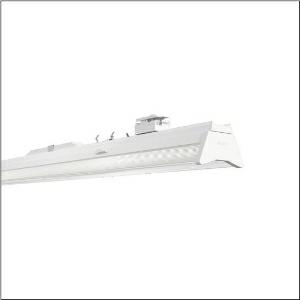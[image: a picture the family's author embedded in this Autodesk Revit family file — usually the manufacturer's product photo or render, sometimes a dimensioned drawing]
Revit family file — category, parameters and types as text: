
# Revit family: licross_21_performance_mo_52tm16dn445g
name_source: partatom
category: Lighting Fixtures
units: mm (PartAtom-declared; Revit-internal decimal feet)

## family parameters
Cut with Voids When Loaded = No
Host = Face
Light Source = No
Part Type = Normal
Room Calculation Point = No
Round Connector Dimension = Use Diameter
Shared = No

## types (1)
- --- (1 x LED, 4500 lm, 24.9 W, 4000K)
    Apparent Load = 25 VA
    CIE Flux Codes = 66 88 96 79 100
    Color Rendering = 80
    Color Temperature = 4000K
    Default Elevation = 1800 mm
    Description = Licross 21 Performance MO, luminaire insert, of sheet steel, galvanised, coil coated, white, length: 1.500mm, width: 120mm, height: 123mm, LED rated luminous flux: 4.500lm, light colour: 840, SDCM (Standard Deviation of Colour Matching)MacAdam ≤ 3 SDCM (initial), control gear: DALI 2, with plug, 5-pole, with phase selection, mains connection: 220..240V, AC, 50/60Hz, rated input power: 25W, internal wiring halogen-free, primary light control with lens, of plastic, primary optical cover: cover, of PMMA, CAT 2 (L<= 3000cd/m²), light emission: direct/indirect distribution, primary light characteristic: symmetric, protection rating (complete): IP40, insulation class (complete): insulation class I (protective earthing), certification: CE, ENEC, UKCA, protection symbol: D if used in an environment without relevant dust loads with corresponding accessories, impact resistance: IK06, permissible ambient temperature for indoor applications: -25..+50°C, corresponds to IFS (International Featured Standards) requirements for safety and quality in the food industry, reducing of maximum allowable ambient temperature of 5°C with ceiling mounting, LABS conformity tested according to VDMA 24364:2018-05, The light source and the operating device comply with the requirements of the Ecodesign Regulation (EU) 2019/2020 and are replaceable in accordance with this regulation, packaging unit: 1 piece
    Height = 114 mm
    Lamp = 1 x LED
    Lamp Light Flux = 4500 lm
    Lamp Power = 24.9 W
    Lamp count = 1
    Length = 1500 mm
    Luminous efficacy = 181 lm/W
    Manufacturer = Siteco
    ModVariant = No
    Model = 52TM16DN445G
    Mounting Place = Ceiling
    Mounting Type = Pendant
    Number of Poles = 1
    OnlyDefault = Yes
    Power Factor = 1
    Product Name = Licross 21 Performance MO
    Product group = luminaire insert | ceiling pendant
    ProductGroupID = 901
    Protection Class = Protection class I
    Protection Degree = IP 40
    RLX_Detail_Level = 1
    RLX_Emergency_Light_Flux = 0 lm
    RLX_Emergency_Type = 0
    RLX_Emergency_Type_DB = No
    RlxData = <blob elided: 33869 chars, md5=b38eaaeb>
    Socket = socket
    Standby Power = 0 W
    System Light Flux = 4500 lm
    System Power = 25 W
    Type Comments = factory setting: luminous flux: 100 % | dim-lin: 254 | 165 mA
    Type Image = l_1256138.jpg
    URL = http://relux.com
    VarID = @adj_056261
    Voltage = 0 V
    Weight = 0.00 kg
    Width = 120 mm

## geometry (parser evidence)
native form markers: Blend x4, Sweep x11
no freeform markers — native parametric forms only
